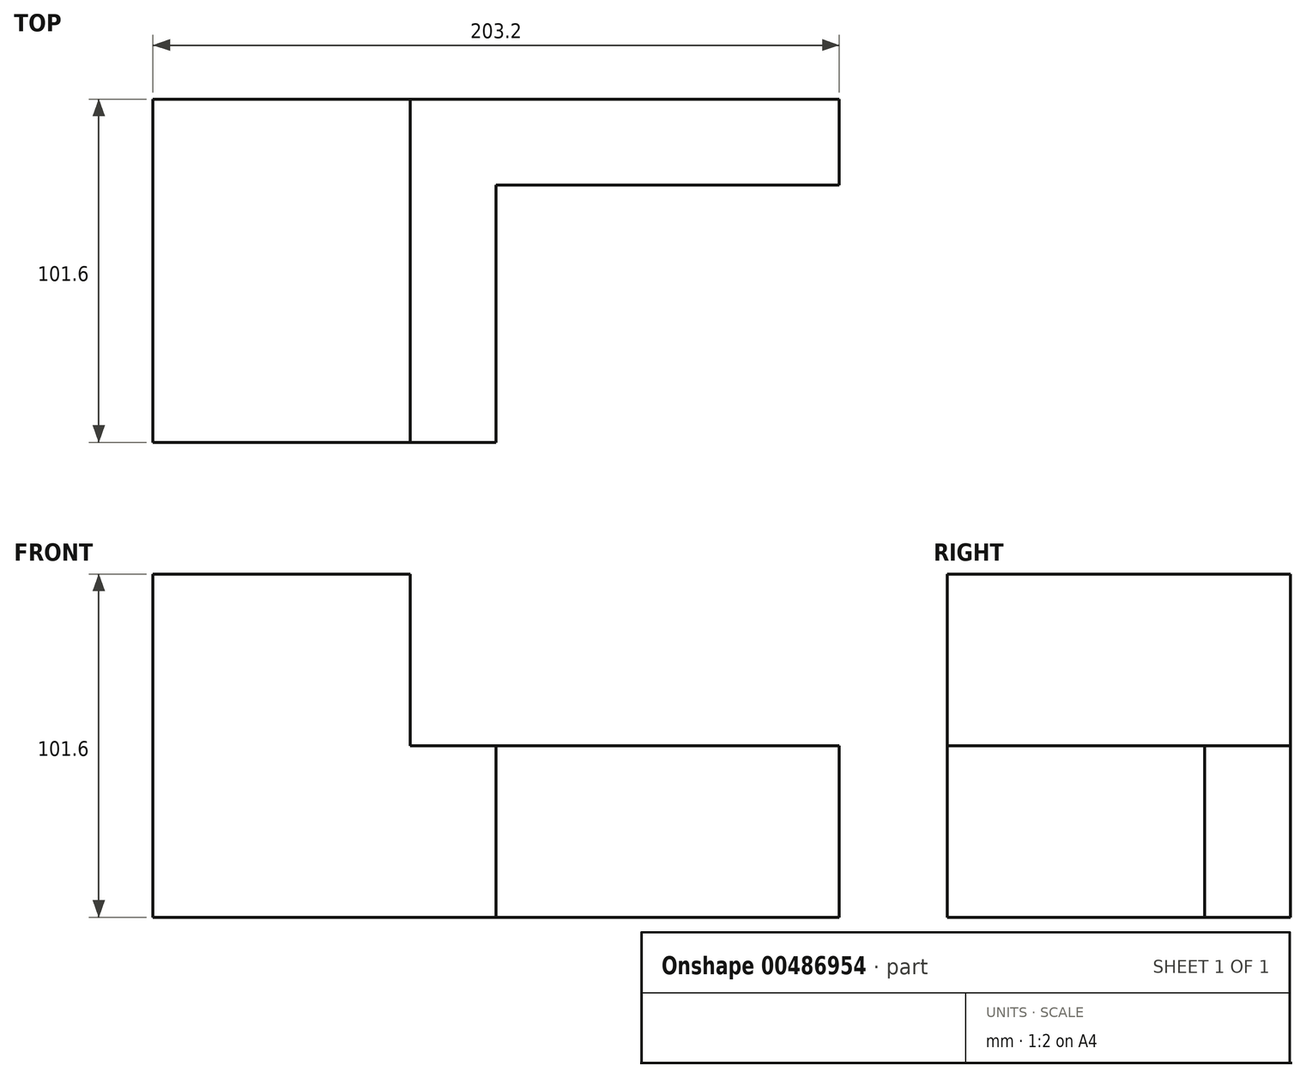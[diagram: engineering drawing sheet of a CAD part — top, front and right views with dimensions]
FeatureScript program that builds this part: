
annotation { "Feature Type Name" : "Feature", "Feature Type Description" : "" }
export const myFeature = defineFeature(function(context is Context, id is Id, definition is map)
    precondition{}
    {
        {
            var Q0;
            Q0=qCreatedBy(makeId("Front.planeOp"),FACE);
            var sketch = newSketch(context, id + "F0", { "sketchPlane" : qUnion([Q0])});
            skLineSegment(sketch, "E0.bottom", {"start": v(-68.58, 101.6) * mm, "end": v(7.62, 101.6) * mm});
            skLineSegment(sketch, "E0.top", {"start": v(-68.58, 0) * mm, "end": v(7.62, 0) * mm});
            skLineSegment(sketch, "E0.left", {"start": v(-68.58, 101.6) * mm, "end": v(-68.58, 0) * mm});
            skLineSegment(sketch, "E0.right", {"start": v(7.62, 101.6) * mm, "end": v(7.62, 50.8) * mm});
            skPoint(sketch, "E1.oppositeSnap0", {"position": v(-68.58, 50.8) * mm});
            skLineSegment(sketch, "E1.bottom", {"start": v(7.62, 0) * mm, "end": v(134.62, 0) * mm});
            skLineSegment(sketch, "E1.top", {"start": v(7.62, 50.8) * mm, "end": v(134.62, 50.8) * mm});
            skLineSegment(sketch, "E1.right", {"start": v(134.62, 0) * mm, "end": v(134.62, 50.8) * mm});
            skSolve(sketch);
        }
        {
            var Q0;
            Q0=makeQuery(id+"F0.imprint","IMPRINT",FACE,{"disambiguationData":[TD([[makeQuery(id+"F0.imprint","IMPRINT",EDGE,{"derivedFrom":sQuery(id+"F0.wireOp",EDGE,"E0.bottom")}),-1.0]])]});
            extrude(context, id + "F1", {"entities" : qUnion([Q0]), "depth" : 101.6 * mm});
        }
        {
            var Q0;
            Q0=makeQuery(id+"F1.opExtrude","SWEPT_FACE",FACE,{"disambiguationData":[OSD([sQuery(id+"F0.wireOp",EDGE,"E1.top")])]});
            var sketch = newSketch(context, id + "F2", { "sketchPlane" : qUnion([Q0])});
            skLineSegment(sketch, "E2.bottom", {"start": v(134.62, -101.6) * mm, "end": v(33.02, -101.6) * mm});
            skLineSegment(sketch, "E2.top", {"start": v(134.62, -25.4) * mm, "end": v(33.02, -25.4) * mm});
            skLineSegment(sketch, "E2.left", {"start": v(134.62, -101.6) * mm, "end": v(134.62, -25.4) * mm});
            skLineSegment(sketch, "E2.right", {"start": v(33.02, -101.6) * mm, "end": v(33.02, -25.4) * mm});
            skSolve(sketch);
        }
        {
            var Q0;
            Q0=makeQuery(id+"F2.imprint","IMPRINT",FACE,{"disambiguationData":[TD([[makeQuery(id+"F2.imprint","IMPRINT",EDGE,{"derivedFrom":sQuery(id+"F2.wireOp",EDGE,"E2.bottom")}),1.0]])]});
            extrude(context, id + "F3", {"entities" : qUnion([Q0]), "operationType" : NewBodyOperationType.REMOVE, "oppositeDirection" : true, "depth" : 50.8 * mm});
        }
    });
